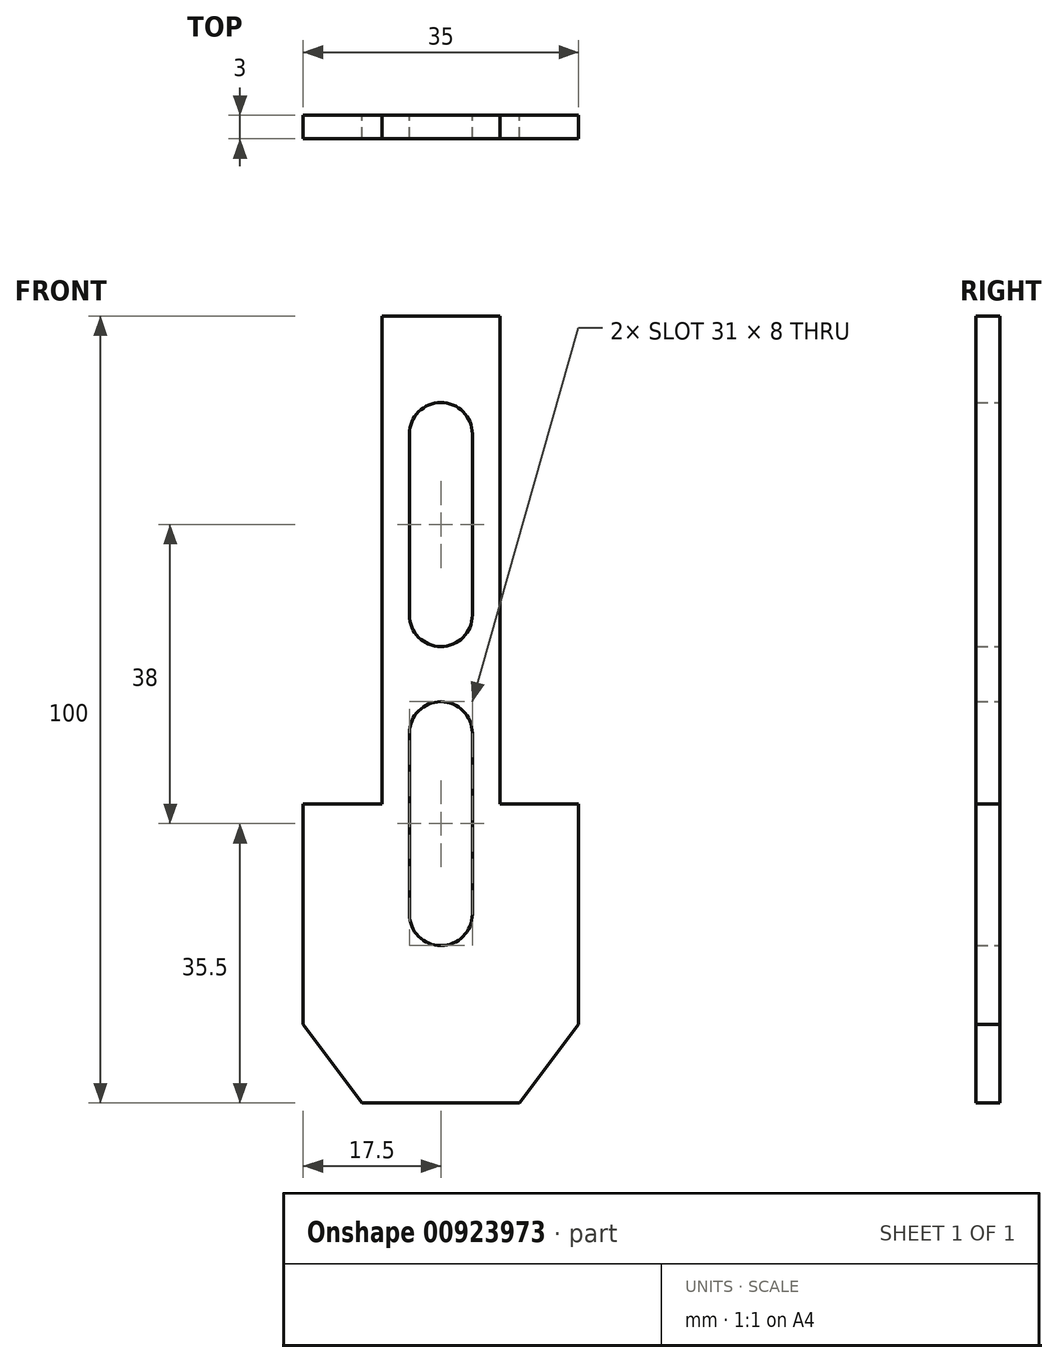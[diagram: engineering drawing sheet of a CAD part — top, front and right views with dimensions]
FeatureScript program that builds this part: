
annotation { "Feature Type Name" : "Feature", "Feature Type Description" : "" }
export const myFeature = defineFeature(function(context is Context, id is Id, definition is map)
    precondition{}
    {
        {
            var Q0;
            Q0=qCreatedBy(makeId("Front.planeOp"),FACE);
            var sketch = newSketch(context, id + "F0", { "sketchPlane" : qUnion([Q0])});
            skLineSegment(sketch, "E0.bottom", {"start": v(17.5, 45) * mm, "end": v(-17.5, 45) * mm});
            skLineSegment(sketch, "E0.left", {"start": v(17.5, 45) * mm, "end": v(17.5, -45) * mm});
            skLineSegment(sketch, "E0.right", {"start": v(-17.5, 45) * mm, "end": v(-17.5, -45) * mm});
            skPoint(sketch, "E0.middle", {"position": v(0, 0) * mm});
            skLineSegment(sketch, "E1", {"start": v(-17.5, -45) * mm, "end": v(-10, -55) * mm});
            skLineSegment(sketch, "E2", {"start": v(-10, -55) * mm, "end": v(10, -55) * mm});
            skLineSegment(sketch, "E3", {"start": v(10, -55) * mm, "end": v(17.5, -45) * mm});
            skLineSegment(sketch, "E4", {"start": v(-17.5, -45) * mm, "end": v(17.5, -45) * mm, "construction": true});
            skLineSegment(sketch, "E5", {"start": v(0, -55) * mm, "end": v(0, 45) * mm, "construction": true});
            skLineSegment(sketch, "E6.bottom", {"start": v(0, 3) * mm, "end": v(0, 3) * mm});
            skLineSegment(sketch, "E6.top", {"start": v(0, 34) * mm, "end": v(0, 34) * mm});
            skLineSegment(sketch, "E6.left", {"start": v(4, 7) * mm, "end": v(4, 30) * mm});
            skLineSegment(sketch, "E6.right", {"start": v(-4, 7) * mm, "end": v(-4, 30) * mm});
            skPoint(sketch, "E6.middle", {"position": v(0, 18.5) * mm});
            skLineSegment(sketch, "E7.bottom", {"start": v(0, -35) * mm, "end": v(0, -35) * mm});
            skLineSegment(sketch, "E7.top", {"start": v(0, -4) * mm, "end": v(0, -4) * mm});
            skLineSegment(sketch, "E7.left", {"start": v(4, -31) * mm, "end": v(4, -8) * mm});
            skLineSegment(sketch, "E7.right", {"start": v(-4, -31) * mm, "end": v(-4, -8) * mm});
            skPoint(sketch, "E7.middle", {"position": v(0, -19.5) * mm});
            skPoint(sketch, "E8.visualSharp", {"position": v(-4, 34) * mm});
            skArc(sketch, "E8.filletArc", {"start": v(0, 34) * mm, "mid": v(-2.83, 32.83) * mm, "end": v(-4, 30) * mm});
            skPoint(sketch, "E9.visualSharp", {"position": v(4, 34) * mm});
            skArc(sketch, "E9.filletArc", {"start": v(4, 30) * mm, "mid": v(2.83, 32.83) * mm, "end": v(0, 34) * mm});
            skPoint(sketch, "E10.visualSharp", {"position": v(-4, 3) * mm});
            skArc(sketch, "E10.filletArc", {"start": v(-4, 7) * mm, "mid": v(-2.83, 4.17) * mm, "end": v(0, 3) * mm});
            skPoint(sketch, "E11.visualSharp", {"position": v(4, 3) * mm});
            skArc(sketch, "E11.filletArc", {"start": v(0, 3) * mm, "mid": v(2.83, 4.17) * mm, "end": v(4, 7) * mm});
            skPoint(sketch, "E12.visualSharp", {"position": v(-4, -4) * mm});
            skArc(sketch, "E12.filletArc", {"start": v(0, -4) * mm, "mid": v(-2.83, -5.17) * mm, "end": v(-4, -8) * mm});
            skPoint(sketch, "E13.visualSharp", {"position": v(4, -4) * mm});
            skArc(sketch, "E13.filletArc", {"start": v(4, -8) * mm, "mid": v(2.83, -5.17) * mm, "end": v(0, -4) * mm});
            skPoint(sketch, "E14.visualSharp", {"position": v(4, -35) * mm});
            skArc(sketch, "E14.filletArc", {"start": v(0, -35) * mm, "mid": v(2.83, -33.83) * mm, "end": v(4, -31) * mm});
            skPoint(sketch, "E15.visualSharp", {"position": v(-4, -35) * mm});
            skArc(sketch, "E15.filletArc", {"start": v(-4, -31) * mm, "mid": v(-2.83, -33.83) * mm, "end": v(0, -35) * mm});
            skSolve(sketch);
        }
        {
            var Q0;
            Q0=makeQuery(id+"F0.imprint","IMPRINT",FACE,{"disambiguationData":[TD([[makeQuery(id+"F0.imprint","IMPRINT",EDGE,{"derivedFrom":sQuery(id+"F0.wireOp",EDGE,"E0.bottom")}),1.0]])]});
            extrude(context, id + "F1", {"entities" : qUnion([Q0]), "depth" : 3 * mm, "offsetDistance" : 25 * mm});
        }
        {
            var Q0;
            Q0=makeQuery(id+"F1.opExtrude","CAP_FACE",FACE,{"disambiguationData":[OSD([sQuery(id+"F0.wireOp",EDGE,"E0.bottom"),sQuery(id+"F0.wireOp",EDGE,"E0.left"),sQuery(id+"F0.wireOp",EDGE,"E0.right"),sQuery(id+"F0.wireOp",EDGE,"E1"),sQuery(id+"F0.wireOp",EDGE,"E2"),sQuery(id+"F0.wireOp",EDGE,"E3"),sQuery(id+"F0.wireOp",EDGE,"E6.left"),sQuery(id+"F0.wireOp",EDGE,"E6.right"),sQuery(id+"F0.wireOp",EDGE,"E7.left"),sQuery(id+"F0.wireOp",EDGE,"E7.right"),sQuery(id+"F0.wireOp",EDGE,"E8.filletArc"),sQuery(id+"F0.wireOp",EDGE,"E9.filletArc"),sQuery(id+"F0.wireOp",EDGE,"E10.filletArc"),sQuery(id+"F0.wireOp",EDGE,"E11.filletArc"),sQuery(id+"F0.wireOp",EDGE,"E12.filletArc"),sQuery(id+"F0.wireOp",EDGE,"E13.filletArc"),sQuery(id+"F0.wireOp",EDGE,"E14.filletArc"),sQuery(id+"F0.wireOp",EDGE,"E15.filletArc")])],"isStart":false});
            var sketch = newSketch(context, id + "F2", { "sketchPlane" : qUnion([Q0])});
            skLineSegment(sketch, "E16.bottom", {"start": v(-17.5, 45) * mm, "end": v(-7.5, 45) * mm});
            skLineSegment(sketch, "E16.top", {"start": v(-17.5, -17) * mm, "end": v(-7.5, -17) * mm});
            skLineSegment(sketch, "E16.left", {"start": v(-17.5, 45) * mm, "end": v(-17.5, -17) * mm});
            skLineSegment(sketch, "E16.right", {"start": v(-7.5, 45) * mm, "end": v(-7.5, -17) * mm});
            skLineSegment(sketch, "E17.bottom", {"start": v(17.5, 45) * mm, "end": v(7.5, 45) * mm});
            skLineSegment(sketch, "E17.top", {"start": v(17.5, -17) * mm, "end": v(7.5, -17) * mm});
            skLineSegment(sketch, "E17.left", {"start": v(17.5, 45) * mm, "end": v(17.5, -17) * mm});
            skLineSegment(sketch, "E17.right", {"start": v(7.5, 45) * mm, "end": v(7.5, -17) * mm});
            skSolve(sketch);
        }
        {
            var Q0;
            Q0=makeQuery(id+"F2.imprint","IMPRINT",FACE,{"disambiguationData":[TD([[makeQuery(id+"F2.imprint","IMPRINT",EDGE,{"derivedFrom":sQuery(id+"F2.wireOp",EDGE,"E16.bottom")}),1.0]])]});
            var Q1;
            Q1=makeQuery(id+"F2.imprint","IMPRINT",FACE,{"disambiguationData":[TD([[makeQuery(id+"F2.imprint","IMPRINT",EDGE,{"derivedFrom":sQuery(id+"F2.wireOp",EDGE,"E17.bottom")}),1.0]])]});
            extrude(context, id + "F3", {"entities" : qUnion([Q0, Q1]), "operationType" : NewBodyOperationType.REMOVE, "oppositeDirection" : true, "depth" : 25 * mm, "offsetDistance" : 25 * mm});
        }
    });
